# Revit family: EqualDoor1VPNFR
name_source: partatom
category: Doors
revit_build: Autodesk Revit 2014 (Build: 20130308_1515(x64)
units: mm (PartAtom-declared; Revit-internal decimal feet)

## types (1)
- EqualDoor1VPNFR
    Analytic Construction = <None>
    Cost = 0 $
    Description = Equal Door 1 Vision Panel NFR
    DoorCore = Insulation
    DoorFacingSpecies = DoorMaterial
    DoorFacingType = Polyurethane
    DoorTolerance = 3 mm  [stored 0.00984252 ft]
    DurationUnit = years
    ExpectedLife = years
    Fire Rating = NFR
    FireRating = NFR
    FrameMaterial = FrameMaterial
    FrameThickness = 50 mm  [stored 0.164042 ft]
    Function = Interior
    HeadTolerance = 5 mm  [stored 0.0164042 ft]
    Height = 2000 mm  [stored 6.56168 ft]
    Hingle/PivotType = Tension adjustable Zinc plated Steel double action hinge with self lubricating enclosed high
tensile springs
    JambTolerance = 5 mm  [stored 0.0164042 ft]
    Manufacturer = Kenfield
    ManufacturerName = Kenfield
    Material = Polyurethane
    NBSDescription = Equal Door 1 Vision Panel NFR
    NominalHeight = 0 mm  [stored 0 ft]
    NominalLength = 0 mm  [stored 0 ft]
    NominalWidth = 0 mm  [stored 0 ft]
    Rough Height = 0 mm  [stored 0 ft]
    Rough Width = 0 mm  [stored 0 ft]
    Thickness = 0 mm  [stored 0 ft]
    URL = www.kenfield.com
    VPRadius = 25 mm  [stored 0.082021 ft]
    Version = 1
    VisionPanelFromFFL = 1200 mm
    VisionPanelFromLockEdge = 179 mm
    VisionPanelHeight = 600 mm
    VisionPanelWidth = 200 mm
    Wall Closure = By host
    Width = 1000 mm  [stored 3.28084 ft]

note: [stored X ft] marks values corroborated as IEEE doubles in the binary element streams (Revit-internal decimal feet)

## geometry (parser evidence)
native form markers: Sweep x1
no freeform markers — native parametric forms only
